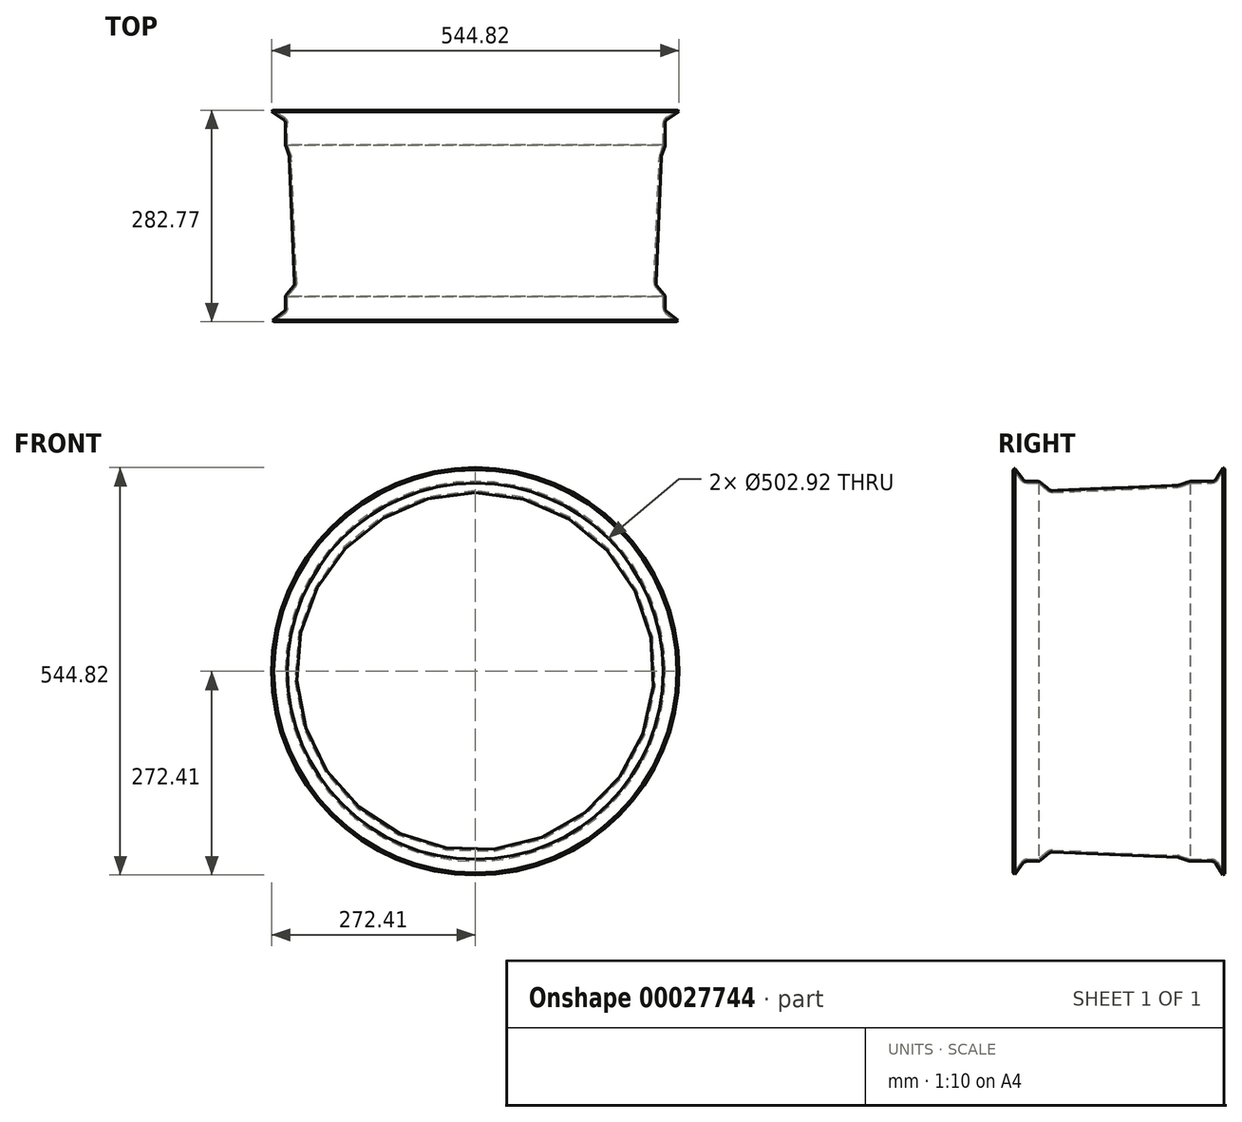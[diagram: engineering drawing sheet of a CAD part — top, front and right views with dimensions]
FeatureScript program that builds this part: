
annotation { "Feature Type Name" : "Feature", "Feature Type Description" : "" }
export const myFeature = defineFeature(function(context is Context, id is Id, definition is map)
    precondition{}
    {
        {
            var Q0;
            Q0=qCreatedBy(makeId("Right.planeOp"),FACE);
            var sketch = newSketch(context, id + "F0", { "sketchPlane" : qUnion([Q0])});
            skLineSegment(sketch, "E0", {"start": v(-123.86, 254) * mm, "end": v(-109.52, 254) * mm, "construction": true});
            skLineSegment(sketch, "E1", {"start": v(0, 0) * mm, "end": v(0, 254) * mm, "construction": true});
            skPoint(sketch, "E1.endSnap0", {"position": v(0, 254) * mm});
            skLineSegment(sketch, "E2", {"start": v(-140.14, 271.25) * mm, "end": v(-128.9, 256.5) * mm});
            skLineSegment(sketch, "E3", {"start": v(-105.46, 252.53) * mm, "end": v(-94.14, 243.13) * mm});
            skLineSegment(sketch, "E4", {"start": v(-89.81, 241.67) * mm, "end": v(77.91, 248.76) * mm});
            skLineSegment(sketch, "E5", {"start": v(79.7, 249.1) * mm, "end": v(93.05, 253.66) * mm});
            skLineSegment(sketch, "E6", {"start": v(95.1, 254) * mm, "end": v(123.47, 254) * mm});
            skLineSegment(sketch, "E7", {"start": v(128.86, 257) * mm, "end": v(138.45, 272.41) * mm});
            skPoint(sketch, "E8.visualSharp", {"position": v(-127, 254) * mm});
            skArc(sketch, "E8.filletArc", {"start": v(-128.9, 256.5) * mm, "mid": v(-126.67, 254.66) * mm, "end": v(-123.86, 254) * mm});
            skPoint(sketch, "E9.newPointA", {"position": v(127, 254) * mm});
            skArc(sketch, "E9.filletArc", {"start": v(-105.46, 252.53) * mm, "mid": v(-107.36, 253.62) * mm, "end": v(-109.52, 254) * mm});
            skPoint(sketch, "E10.visualSharp", {"position": v(-92.26, 241.57) * mm});
            skArc(sketch, "E10.filletArc", {"start": v(-94.14, 243.13) * mm, "mid": v(-92.11, 242) * mm, "end": v(-89.81, 241.67) * mm});
            skPoint(sketch, "E11.visualSharp", {"position": v(78.83, 248.8) * mm});
            skArc(sketch, "E11.filletArc", {"start": v(77.91, 248.76) * mm, "mid": v(78.82, 248.86) * mm, "end": v(79.7, 249.1) * mm});
            skPoint(sketch, "E12.visualSharp", {"position": v(94.04, 254) * mm});
            skArc(sketch, "E12.filletArc", {"start": v(95.1, 254) * mm, "mid": v(94.06, 253.91) * mm, "end": v(93.05, 253.66) * mm});
            skArc(sketch, "E13.filletArc", {"start": v(123.47, 254) * mm, "mid": v(126.56, 254.8) * mm, "end": v(128.86, 257) * mm});
            skSolve(sketch);
        }
        {
            var Q0;
            Q0=qCreatedBy(makeId("Right.planeOp"),FACE);
            var sketch = newSketch(context, id + "F1", { "sketchPlane" : qUnion([Q0])});
            skLineSegment(sketch, "E14.0", {"start": v(131.02, 255.65) * mm, "end": v(140.61, 271.07) * mm});
            skLineSegment(sketch, "E14.1", {"start": v(-108.14, 251.46) * mm, "end": v(-95.76, 241.18) * mm});
            skLineSegment(sketch, "E14.2", {"start": v(-123.86, 251.46) * mm, "end": v(-108.14, 251.46) * mm});
            skArc(sketch, "E14.3", {"start": v(-130.93, 254.96) * mm, "mid": v(-127.8, 252.38) * mm, "end": v(-123.86, 251.46) * mm});
            skLineSegment(sketch, "E14.4", {"start": v(-142.16, 269.7) * mm, "end": v(-130.93, 254.96) * mm});
            skArc(sketch, "E14.5", {"start": v(-95.76, 241.18) * mm, "mid": v(-92.93, 239.6) * mm, "end": v(-89.7, 239.13) * mm});
            skLineSegment(sketch, "E14.6", {"start": v(-89.7, 239.13) * mm, "end": v(78.02, 246.22) * mm});
            skArc(sketch, "E14.7", {"start": v(78.02, 246.22) * mm, "mid": v(79.29, 246.37) * mm, "end": v(80.52, 246.7) * mm});
            skLineSegment(sketch, "E14.8", {"start": v(80.52, 246.7) * mm, "end": v(94.47, 251.46) * mm});
            skLineSegment(sketch, "E14.9", {"start": v(94.47, 251.46) * mm, "end": v(123.47, 251.46) * mm});
            skArc(sketch, "E14.10", {"start": v(123.47, 251.46) * mm, "mid": v(127.79, 252.58) * mm, "end": v(131.02, 255.65) * mm});
            skLineSegment(sketch, "E15.0", {"start": v(-105.46, 252.53) * mm, "end": v(-94.14, 243.13) * mm});
            skLineSegment(sketch, "E15.1", {"start": v(-140.14, 271.25) * mm, "end": v(-128.9, 256.5) * mm});
            skArc(sketch, "E15.2", {"start": v(-128.9, 256.5) * mm, "mid": v(-126.67, 254.66) * mm, "end": v(-123.86, 254) * mm});
            skLineSegment(sketch, "E15.3", {"start": v(-123.86, 254) * mm, "end": v(-109.52, 254) * mm});
            skArc(sketch, "E15.4", {"start": v(-105.46, 252.53) * mm, "mid": v(-107.36, 253.62) * mm, "end": v(-109.52, 254) * mm});
            skPoint(sketch, "E15.5", {"position": v(-92.26, 241.57) * mm});
            skArc(sketch, "E15.6", {"start": v(-94.14, 243.13) * mm, "mid": v(-92.11, 242) * mm, "end": v(-89.81, 241.67) * mm});
            skLineSegment(sketch, "E15.7", {"start": v(-89.81, 241.67) * mm, "end": v(77.91, 248.76) * mm});
            skLineSegment(sketch, "E15.8", {"start": v(128.86, 257) * mm, "end": v(138.45, 272.41) * mm});
            skArc(sketch, "E15.9", {"start": v(123.47, 254) * mm, "mid": v(126.56, 254.8) * mm, "end": v(128.86, 257) * mm});
            skLineSegment(sketch, "E15.10", {"start": v(95.1, 254) * mm, "end": v(123.47, 254) * mm});
            skArc(sketch, "E15.11", {"start": v(95.1, 254) * mm, "mid": v(94.06, 253.91) * mm, "end": v(93.05, 253.66) * mm});
            skLineSegment(sketch, "E15.12", {"start": v(79.7, 249.1) * mm, "end": v(93.05, 253.66) * mm});
            skArc(sketch, "E15.13", {"start": v(77.91, 248.76) * mm, "mid": v(78.82, 248.86) * mm, "end": v(79.7, 249.1) * mm});
            skLineSegment(sketch, "E16", {"start": v(-140.14, 271.25) * mm, "end": v(-142.16, 269.7) * mm});
            skLineSegment(sketch, "E17", {"start": v(138.45, 272.41) * mm, "end": v(140.61, 271.07) * mm});
            skLineSegment(sketch, "E18", {"start": v(0, 0) * mm, "end": v(-132.17, 0) * mm, "construction": true});
            skSolve(sketch);
        }
        {
            var Q0;
            Q0=makeQuery(id+"F1.imprint","IMPRINT",FACE,{"disambiguationData":[TD([[makeQuery(id+"F1.imprint","IMPRINT",EDGE,{"derivedFrom":sQuery(id+"F1.wireOp",EDGE,"E14.0")}),1.0]])]});
            var Q1;
            Q1 = qConstructionFilter(qBodyType(qCreatedBy(id + "F1" ,EDGE), BodyType.WIRE), ConstructionObject.NO);
            var Q2;
            Q2=sQuery(id+"F1.wireOp",EDGE,"E18");
            revolve(context, id + "F2", {"entities" : qUnion([Q0]), "surfaceEntities" : qUnion([Q1]), "axis" : qUnion([Q2]), "revolveType" : RevolveType.FULL});
        }
    });
